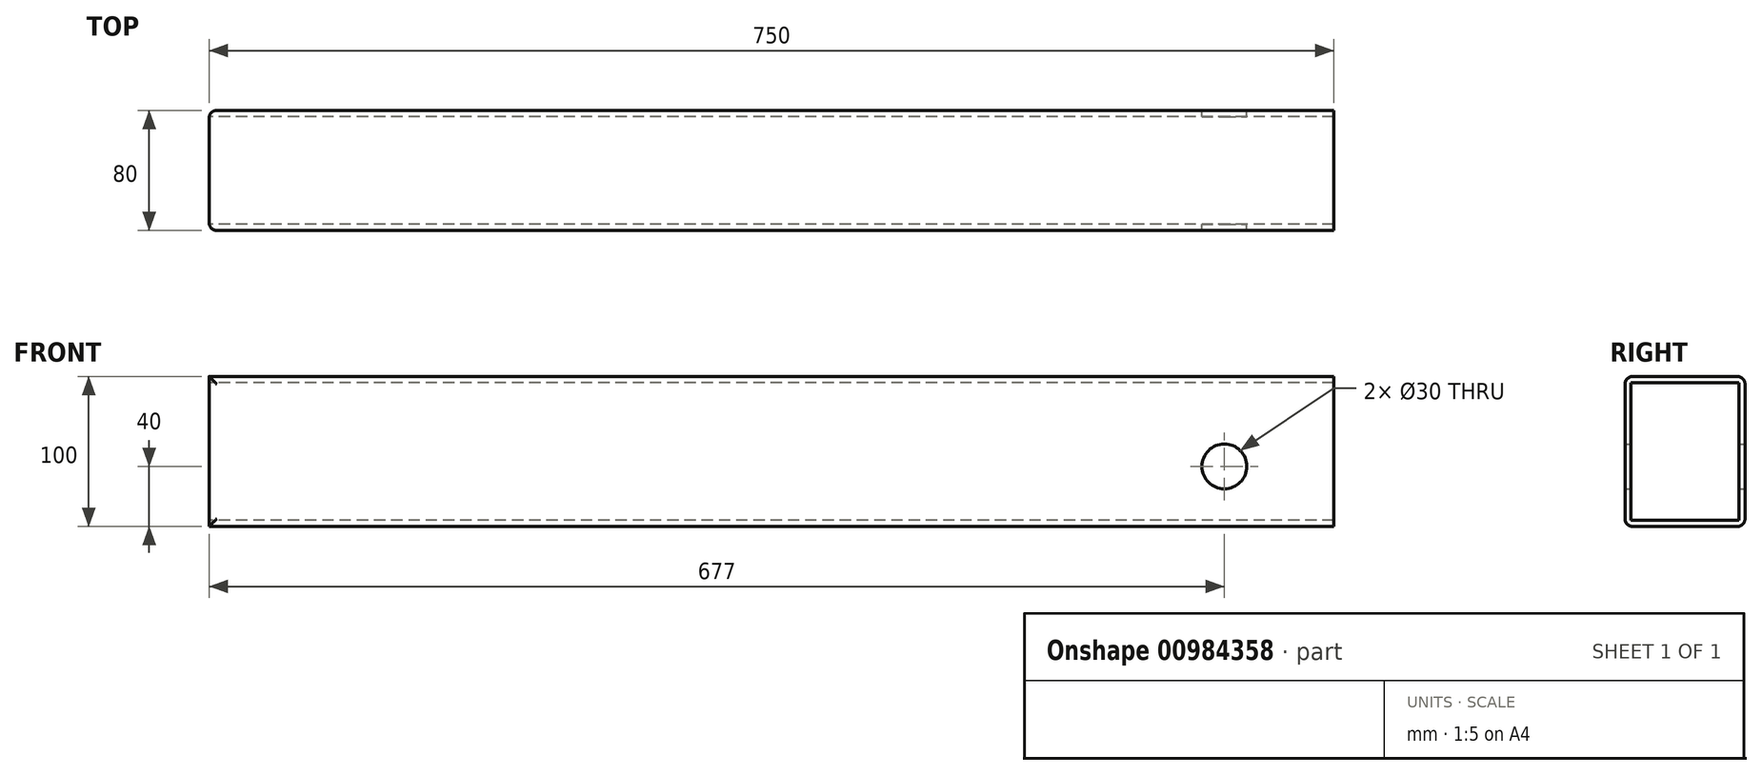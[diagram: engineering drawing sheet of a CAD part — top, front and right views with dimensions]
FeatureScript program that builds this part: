
annotation { "Feature Type Name" : "Feature", "Feature Type Description" : "" }
export const myFeature = defineFeature(function(context is Context, id is Id, definition is map)
    precondition{}
    {
        {
            var Q0;
            Q0=qCreatedBy(makeId("Front.planeOp"),FACE);
            var sketch = newSketch(context, id + "F0", { "sketchPlane" : qUnion([Q0])});
            skLineSegment(sketch, "E0.bottom", {"start": v(375, -50) * mm, "end": v(-375, -50) * mm});
            skLineSegment(sketch, "E0.top", {"start": v(375, 50) * mm, "end": v(-375, 50) * mm});
            skLineSegment(sketch, "E0.left", {"start": v(375, -50) * mm, "end": v(375, 50) * mm});
            skLineSegment(sketch, "E0.right", {"start": v(-375, -50) * mm, "end": v(-375, 50) * mm});
            skPoint(sketch, "E0.middle", {"position": v(0, 0) * mm});
            skPoint(sketch, "E1.visualSharp", {"position": v(-375, 50) * mm});
            skArc(sketch, "E1.filletArc", {"start": v(-375, 50) * mm, "mid": v(-375, 50) * mm, "end": v(-375, 50) * mm});
            skPoint(sketch, "E2.visualSharp", {"position": v(-375, -50) * mm});
            skArc(sketch, "E2.filletArc", {"start": v(-375, -50) * mm, "mid": v(-375, -50) * mm, "end": v(-375, -50) * mm});
            skSolve(sketch);
        }
        {
            var Q0;
            Q0=makeQuery(id+"F0.imprint","IMPRINT",FACE,{"disambiguationData":[TD([[makeQuery(id+"F0.imprint","IMPRINT",EDGE,{"derivedFrom":sQuery(id+"F0.wireOp",EDGE,"E0.bottom")}),-1.0]])]});
            extrude(context, id + "F1", {"entities" : qUnion([Q0]), "depth" : 80 * mm, "offsetDistance" : 25 * mm});
        }
        {
            var Q0;
            Q0=makeQuery(id+"F1.opExtrude","SWEPT_FACE",FACE,{"disambiguationData":[OSD([sQuery(id+"F0.wireOp",EDGE,"E0.right")])]});
            var Q1;
            Q1=makeQuery(id+"F1.opExtrude","SWEPT_FACE",FACE,{"disambiguationData":[OSD([sQuery(id+"F0.wireOp",EDGE,"E0.left")])]});
            shell(context, id + "F2", {"entities" : qUnion([Q0, Q1]), "thickness" : 4 * mm});
        }
        {
            var Q0;
            Q0=makeQuery(id+"F1.opExtrude","CAP_EDGE",EDGE,{"disambiguationData":[OSD([sQuery(id+"F0.wireOp",EDGE,"E0.top")])],"isStart":false});
            var Q1;
            Q1=makeQuery(id+"F1.opExtrude","CAP_EDGE",EDGE,{"disambiguationData":[OSD([sQuery(id+"F0.wireOp",EDGE,"E0.top")])],"isStart":true});
            var Q2;
            Q2=makeQuery(id+"F1.opExtrude","CAP_EDGE",EDGE,{"disambiguationData":[OSD([sQuery(id+"F0.wireOp",EDGE,"E0.bottom")])],"isStart":true});
            var Q3;
            Q3=makeQuery(id+"F1.opExtrude","CAP_EDGE",EDGE,{"disambiguationData":[OSD([sQuery(id+"F0.wireOp",EDGE,"E0.bottom")])],"isStart":false});
            fillet(context, id + "F3", {"entities" : qUnion([Q0, Q1, Q2, Q3]), "radius" : 5 * mm, "tangentPropagation" : true, "allowEdgeOverflow" : false});
        }
        {
            var Q0;
            Q0=qCreatedBy(makeId("Front.planeOp"),FACE);
            var sketch = newSketch(context, id + "F4", { "sketchPlane" : qUnion([Q0])});
            skCircle(sketch, "E3", {"center": v(302, -10) * mm, "radius": 15 * mm});
            skSolve(sketch);
        }
        {
            var Q0;
            Q0=qSketchRegion(id+"F4",true);
            extrude(context, id + "F5", {"entities" : qUnion([Q0]), "operationType" : NewBodyOperationType.REMOVE, "endBound" : BoundingType.THROUGH_ALL, "depth" : 25 * mm, "offsetDistance" : 25 * mm});
        }
    });
